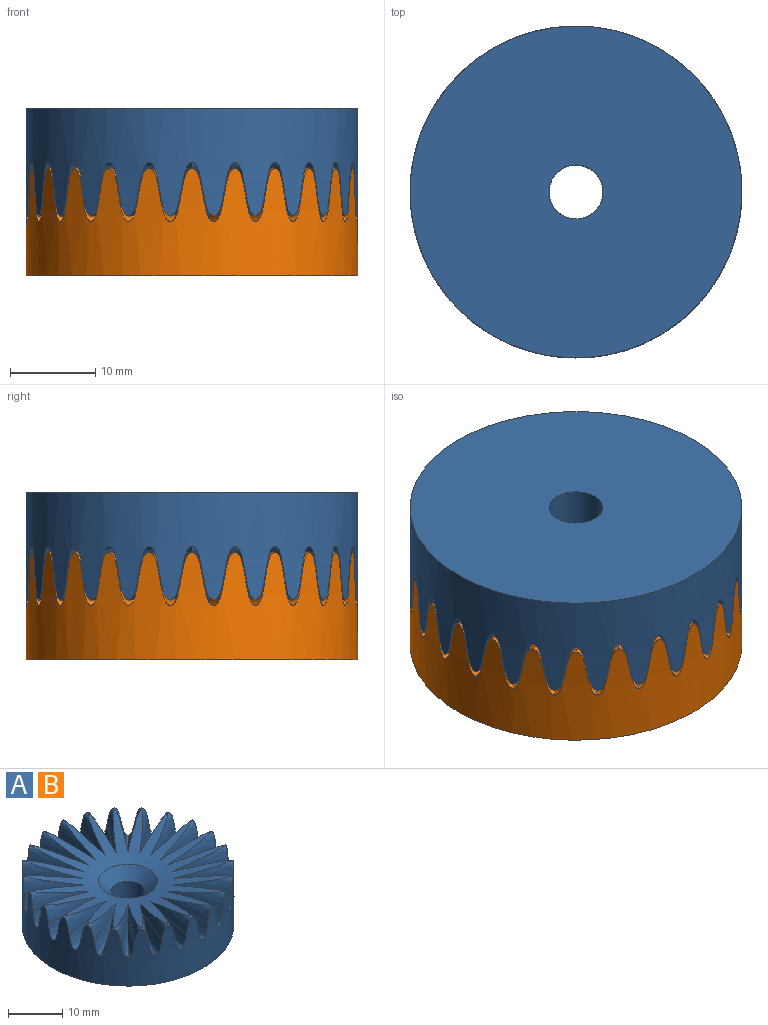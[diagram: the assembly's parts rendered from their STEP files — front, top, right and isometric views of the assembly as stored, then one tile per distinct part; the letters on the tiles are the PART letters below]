
ASSEMBLY  parts=2 mates=1
PART A: 101 faces, bbox 39.3x39.3x12.7 mm
  f0: extruded ~9.8x3.17mm, area 22.8mm2, adj f91,f92,f96
  f1: extruded ~9.46x4.88mm, area 22.8mm2, adj f88,f89,f96
  f2: extruded ~8.48x6.92mm, area 22.8mm2, adj f85,f86,f96
  f3: extruded ~8.48x6.92mm, area 22.8mm2, adj f82,f83,f96
  f4: extruded ~9.46x4.88mm, area 22.8mm2, adj f79,f80,f96
  f5: extruded ~9.8x3.17mm, area 22.8mm2, adj f76,f77,f96
  f6: extruded ~9.8x3.17mm, area 22.8mm2, adj f73,f74,f96
  f7: extruded ~9.46x4.88mm, area 22.8mm2, adj f70,f71,f96
  f8: extruded ~8.48x6.92mm, area 22.8mm2, adj f67,f68,f96
  f9: extruded ~8.48x6.92mm, area 22.8mm2, adj f64,f65,f96
  f10: extruded ~9.46x4.88mm, area 22.8mm2, adj f61,f62,f96
  f11: extruded ~9.8x3.17mm, area 22.8mm2, adj f58,f59,f96
  f12: extruded ~9.8x3.17mm, area 22.8mm2, adj f55,f56,f96
  f13: extruded ~9.46x4.88mm, area 22.8mm2, adj f52,f53,f96
  f14: extruded ~8.48x6.92mm, area 22.8mm2, adj f49,f50,f96
  f15: extruded ~8.48x6.92mm, area 22.8mm2, adj f46,f47,f96
  f16: extruded ~9.46x4.88mm, area 22.8mm2, adj f43,f44,f96
  f17: extruded ~9.8x3.17mm, area 22.8mm2, adj f40,f41,f96
  f18: extruded ~9.8x3.17mm, area 22.8mm2, adj f37,f38,f96
  f19: extruded ~9.46x4.88mm, area 22.8mm2, adj f34,f35,f96
  f20: extruded ~8.48x6.92mm, area 22.8mm2, adj f31,f32,f96
  f21: extruded ~8.48x6.92mm, area 22.8mm2, adj f28,f29,f96
  f22: extruded ~9.46x4.88mm, area 22.8mm2, adj f25,f26,f96
  f23: extruded ~9.46x4.88mm, area 22.8mm2, adj f24,f94,f96
  f24: extruded ~10.78x5.45mm, area 23.8mm2, adj f23,f25,f95,f96,f97
  f25: extruded ~10.78x5.45mm, area 23.8mm2, adj f22,f24,f27,f96,f97
  f26: extruded ~8.48x6.92mm, area 22.8mm2, adj f22,f27,f96
  f27: extruded ~9.62x7.8mm, area 23.8mm2, adj f25,f26,f28,f96,f97
  f28: extruded ~9.62x7.8mm, area 23.8mm2, adj f21,f27,f30,f96,f97
  f29: extruded ~8.48x6.92mm, area 22.8mm2, adj f21,f30,f96
  f30: extruded ~9.62x7.8mm, area 23.8mm2, adj f28,f29,f31,f96,f97
  f31: extruded ~9.62x7.8mm, area 23.8mm2, adj f20,f30,f33,f96,f97
  f32: extruded ~9.46x4.88mm, area 22.8mm2, adj f20,f33,f96
  f33: extruded ~10.78x5.45mm, area 23.8mm2, adj f31,f32,f34,f96,f97
  f34: extruded ~10.78x5.45mm, area 23.8mm2, adj f19,f33,f36,f96,f97
  f35: extruded ~9.8x3.17mm, area 22.8mm2, adj f19,f36,f96
  f36: extruded ~11.21x3.18mm, area 23.8mm2, adj f34,f35,f37,f96,f97
  f37: extruded ~11.21x3.18mm, area 23.8mm2, adj f18,f36,f39,f96,f97
  f38: extruded ~9.8x3.17mm, area 22.8mm2, adj f18,f39,f96
  f39: extruded ~11.21x3.18mm, area 23.8mm2, adj f37,f38,f40,f96,f97
  f40: extruded ~11.21x3.18mm, area 23.8mm2, adj f17,f39,f42,f96,f97
  f41: extruded ~9.46x4.88mm, area 22.8mm2, adj f17,f42,f96
  f42: extruded ~10.78x5.45mm, area 23.8mm2, adj f40,f41,f43,f96,f97
  f43: extruded ~10.78x5.45mm, area 23.8mm2, adj f16,f42,f45,f96,f97
  f44: extruded ~8.48x6.92mm, area 22.8mm2, adj f16,f45,f96
  f45: extruded ~9.62x7.8mm, area 23.8mm2, adj f43,f44,f46,f96,f97
  f46: extruded ~9.62x7.8mm, area 23.8mm2, adj f15,f45,f48,f96,f97
  f47: extruded ~8.48x6.92mm, area 22.8mm2, adj f15,f48,f96
  f48: extruded ~9.62x7.8mm, area 23.8mm2, adj f46,f47,f49,f96,f97
  f49: extruded ~9.62x7.8mm, area 23.8mm2, adj f14,f48,f51,f96,f97
  f50: extruded ~9.46x4.88mm, area 22.8mm2, adj f14,f51,f96
  f51: extruded ~10.78x5.45mm, area 23.8mm2, adj f49,f50,f52,f96,f97
  f52: extruded ~10.78x5.45mm, area 23.8mm2, adj f13,f51,f54,f96,f97
  f53: extruded ~9.8x3.17mm, area 22.8mm2, adj f13,f54,f96
  f54: extruded ~11.21x3.18mm, area 23.8mm2, adj f52,f53,f55,f96,f97
  f55: extruded ~11.21x3.18mm, area 23.8mm2, adj f12,f54,f57,f96,f97
  f56: extruded ~9.8x3.17mm, area 22.8mm2, adj f12,f57,f96
  f57: extruded ~11.21x3.18mm, area 23.8mm2, adj f55,f56,f58,f96,f97
  f58: extruded ~11.21x3.18mm, area 23.8mm2, adj f11,f57,f60,f96,f97
  f59: extruded ~9.46x4.88mm, area 22.8mm2, adj f11,f60,f96
  f60: extruded ~10.78x5.45mm, area 23.8mm2, adj f58,f59,f61,f96,f97
  f61: extruded ~10.78x5.45mm, area 23.8mm2, adj f10,f60,f63,f96,f97
  f62: extruded ~8.48x6.92mm, area 22.8mm2, adj f10,f63,f96
  f63: extruded ~9.62x7.8mm, area 23.8mm2, adj f61,f62,f64,f96,f97
  f64: extruded ~9.62x7.8mm, area 23.8mm2, adj f9,f63,f66,f96,f97
  f65: extruded ~8.48x6.92mm, area 22.8mm2, adj f9,f66,f96
  f66: extruded ~9.62x7.8mm, area 23.8mm2, adj f64,f65,f67,f96,f97
  f67: extruded ~9.62x7.8mm, area 23.8mm2, adj f8,f66,f69,f96,f97
  f68: extruded ~9.46x4.88mm, area 22.8mm2, adj f8,f69,f96
  f69: extruded ~10.78x5.45mm, area 23.8mm2, adj f67,f68,f70,f96,f97
  f70: extruded ~10.78x5.45mm, area 23.8mm2, adj f7,f69,f72,f96,f97
  f71: extruded ~9.8x3.17mm, area 22.8mm2, adj f7,f72,f96
  f72: extruded ~11.21x3.18mm, area 23.8mm2, adj f70,f71,f73,f96,f97
  f73: extruded ~11.21x3.18mm, area 23.8mm2, adj f6,f72,f75,f96,f97
  f74: extruded ~9.8x3.17mm, area 22.8mm2, adj f6,f75,f96
  f75: extruded ~11.21x3.18mm, area 23.8mm2, adj f73,f74,f76,f96,f97
  f76: extruded ~11.21x3.18mm, area 23.8mm2, adj f5,f75,f78,f96,f97
  f77: extruded ~9.46x4.88mm, area 22.8mm2, adj f5,f78,f96
  f78: extruded ~10.78x5.45mm, area 23.8mm2, adj f76,f77,f79,f96,f97
  f79: extruded ~10.78x5.45mm, area 23.8mm2, adj f4,f78,f81,f96,f97
  f80: extruded ~8.48x6.92mm, area 22.8mm2, adj f4,f81,f96
  f81: extruded ~9.62x7.8mm, area 23.8mm2, adj f79,f80,f82,f96,f97
  f82: extruded ~9.62x7.8mm, area 23.8mm2, adj f3,f81,f84,f96,f97
  f83: extruded ~8.48x6.92mm, area 22.8mm2, adj f3,f84,f96
  f84: extruded ~9.62x7.8mm, area 23.8mm2, adj f82,f83,f85,f96,f97
  f85: extruded ~9.62x7.8mm, area 23.8mm2, adj f2,f84,f87,f96,f97
  f86: extruded ~9.46x4.88mm, area 22.8mm2, adj f2,f87,f96
  f87: extruded ~10.78x5.45mm, area 23.8mm2, adj f85,f86,f88,f96,f97
  f88: extruded ~10.78x5.45mm, area 23.8mm2, adj f1,f87,f90,f96,f97
  f89: extruded ~9.8x3.17mm, area 22.8mm2, adj f1,f90,f96
  f90: extruded ~11.21x3.18mm, area 23.8mm2, adj f88,f89,f91,f96,f97
  f91: extruded ~11.21x3.18mm, area 23.8mm2, adj f0,f90,f93,f96,f97
  f92: extruded ~9.8x3.17mm, area 22.8mm2, adj f0,f93,f96
  f93: extruded ~11.21x3.18mm, area 23.8mm2, adj f91,f92,f95,f96,f97
  f94: extruded ~9.8x3.17mm, area 22.8mm2, adj f23,f95,f96
  f95: extruded ~11.21x3.18mm, area 23.8mm2, adj f24,f93,f94,f96,f97
  f96: cylinder r=19.52mm len=39.03mm, axis (0,0,1), area 1170.7mm2, adj f0,f1,f2,f3,f4,f5,f6,f7
  f97: cone r=5.42mm half-angle=78.3deg, axis (0,0,1), area 541.1mm2, adj f24,f25,f27,f28,f30,f31,f33,f34
  f98: cone r=3.17mm half-angle=45deg, axis (0,0,1), area 85.7mm2, adj f97,f100
  f99: plane 39.03x39.03mm, normal (0,0,-1), area 1165mm2, adj f96,f100
  f100: cylinder r=3.17mm len=7.62mm, axis (0,0,-1), area 152mm2, adj f98,f99
PART B: same geometry as A
PLACE A rot(axis=(-0.38,0.92,0),180deg) t=(21.36,11.66,-10.77)mm
PLACE B rot(axis=(0,0,-1),37.5deg) t=(21.36,11.66,-30.5)mm
MATE cylindrical B.f96 <-> A.f96  axis (0,0,1) through (21.36,11.66,-20.63)mm
